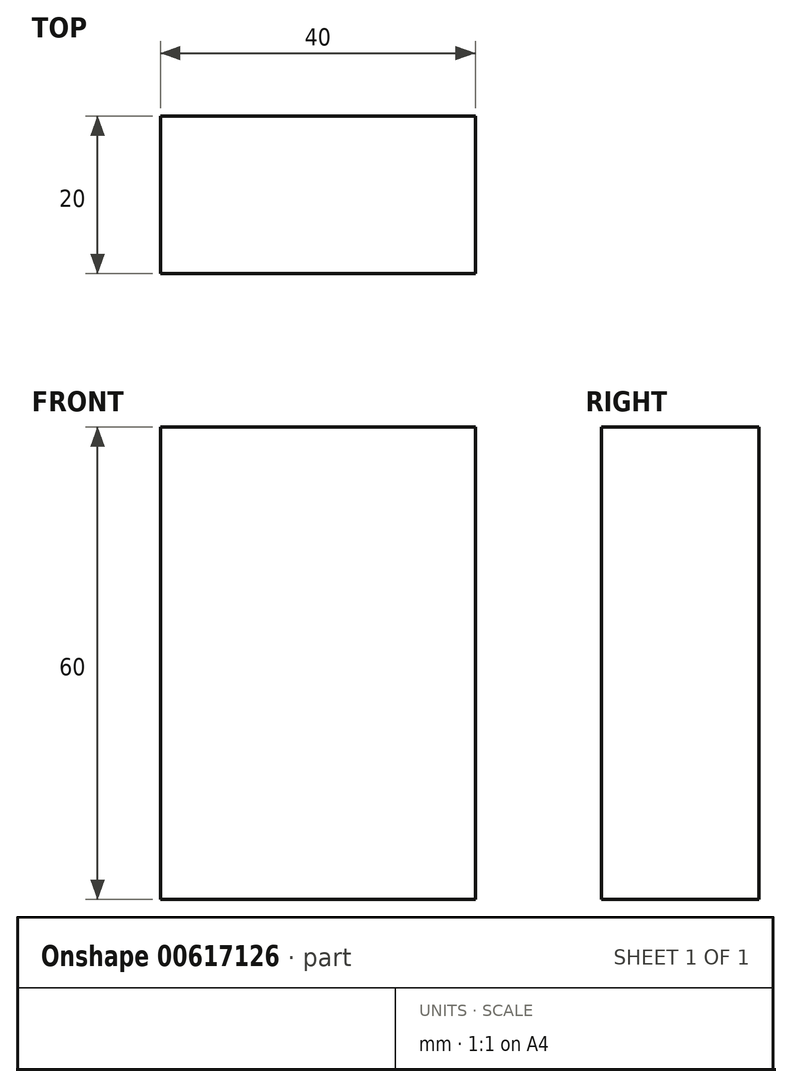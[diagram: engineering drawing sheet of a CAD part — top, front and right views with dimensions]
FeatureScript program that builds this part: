
annotation { "Feature Type Name" : "Feature", "Feature Type Description" : "" }
export const myFeature = defineFeature(function(context is Context, id is Id, definition is map)
    precondition{}
    {
        {
            var Q0;
            Q0=qCreatedBy(makeId("Front.planeOp"),FACE);
            var sketch = newSketch(context, id + "F0", { "sketchPlane" : qUnion([Q0])});
            skLineSegment(sketch, "E0", {"start": v(-40, 20.73) * mm, "end": v(0, 20.73) * mm});
            skLineSegment(sketch, "E1", {"start": v(-40, 20.73) * mm, "end": v(-40, -39.27) * mm});
            skLineSegment(sketch, "E2", {"start": v(-40, -39.27) * mm, "end": v(0, -39.27) * mm});
            skLineSegment(sketch, "E3", {"start": v(0, -39.27) * mm, "end": v(0, 20.73) * mm});
            skSolve(sketch);
        }
        {
            var Q0;
            Q0 = qSketchRegion(id + "F0", true);
            extrude(context, id + "F1", {"entities" : qUnion([Q0]), "depth" : 20 * mm, "offsetDistance" : 25 * mm});
        }
    });
